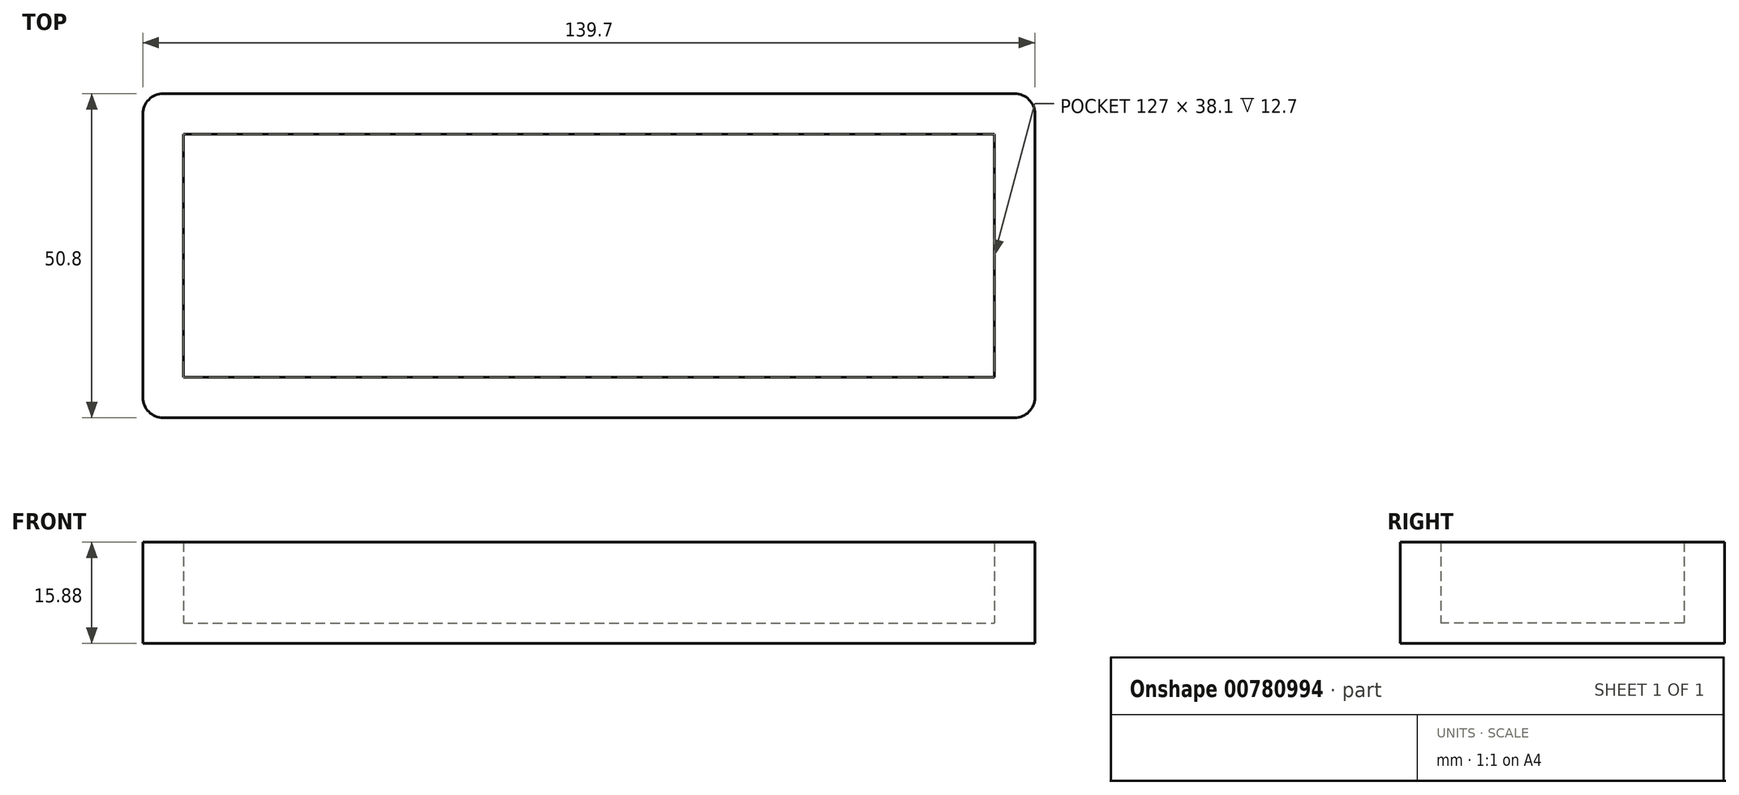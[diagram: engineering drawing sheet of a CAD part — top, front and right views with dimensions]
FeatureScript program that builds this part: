
annotation { "Feature Type Name" : "Feature", "Feature Type Description" : "" }
export const myFeature = defineFeature(function(context is Context, id is Id, definition is map)
    precondition{}
    {
        {
            var Q0;
            Q0=qCreatedBy(makeId("Top.planeOp"),FACE);
            var sketch = newSketch(context, id + "F0", { "sketchPlane" : qUnion([Q0])});
            skLineSegment(sketch, "E0.bottom", {"start": v(-64.83, 16.35) * mm, "end": v(74.87, 16.35) * mm});
            skLineSegment(sketch, "E0.top", {"start": v(-64.83, -34.45) * mm, "end": v(74.87, -34.45) * mm});
            skLineSegment(sketch, "E0.left", {"start": v(-64.83, 16.35) * mm, "end": v(-64.83, -34.45) * mm});
            skLineSegment(sketch, "E0.right", {"start": v(74.87, 16.35) * mm, "end": v(74.87, -34.45) * mm});
            skLineSegment(sketch, "E1", {"start": v(-64.83, 10) * mm, "end": v(-58.48, 10) * mm});
            skLineSegment(sketch, "E2", {"start": v(-58.48, 10) * mm, "end": v(-58.48, 16.35) * mm});
            skLineSegment(sketch, "E3", {"start": v(-58.48, 10) * mm, "end": v(74.87, 10) * mm});
            skLineSegment(sketch, "E4", {"start": v(-58.48, 10) * mm, "end": v(-58.48, -34.45) * mm});
            skLineSegment(sketch, "E5", {"start": v(-64.83, -34.45) * mm, "end": v(-64.83, -28.1) * mm});
            skLineSegment(sketch, "E6", {"start": v(-64.83, -28.1) * mm, "end": v(74.87, -28.1) * mm});
            skLineSegment(sketch, "E7", {"start": v(74.87, 16.35) * mm, "end": v(68.52, 16.35) * mm});
            skLineSegment(sketch, "E8", {"start": v(68.52, 16.35) * mm, "end": v(68.52, -34.45) * mm});
            skLineSegment(sketch, "E9", {"start": v(-58.48, 10) * mm, "end": v(68.52, -28.1) * mm});
            skSolve(sketch);
        }
        {
            var Q0;
            {var subQ0=sQuery(id+"F0.wireOp",EDGE,"E4");var subQ1=sQuery(id+"F0.wireOp",EDGE,"E0.top");var subQ2=makeQuery(id+"F0.imprint","INTERSECT",VERTEX,{"derivedFrom":[subQ1,subQ0]});var subQ15=sQuery(id+"F0.wireOp",EDGE,"E0.right");var subQ16=sQuery(id+"F0.wireOp",EDGE,"E0.bottom");var subQ17=makeQuery(id+"F0.imprint","INTERSECT",VERTEX,{"derivedFrom":[subQ16,subQ15]});var subQ19=sQuery(id+"F0.wireOp",EDGE,"E3");var subQ22=makeQuery(id+"F0.imprint","INTERSECT",VERTEX,{"derivedFrom":[subQ15,subQ19]});var subQ26=sQuery(id+"F0.wireOp",EDGE,"E2");var subQ28=makeQuery(id+"F0.imprint","IMPRINT",EDGE,{"derivedFrom":subQ26});var subQ29=sQuery(id+"F0.wireOp",EDGE,"E1");var subQ33=makeQuery(id+"F0.imprint","IMPRINT",EDGE,{"derivedFrom":subQ29});var subQ34=makeQuery(id+"F0.imprint","INTERSECT",VERTEX,{"derivedFrom":[subQ1,subQ15]});Q0=qUnion([makeQuery(id+"F0.imprint","IMPRINT",FACE,{"disambiguationData":[TD([[makeQuery(id+"F0.imprint","IMPRINT",EDGE,{"disambiguationData":[TD([[subQ34,1.0]])],"derivedFrom":subQ1}),1.0]])]}),makeQuery(id+"F0.imprint","IMPRINT",FACE,{"disambiguationData":[TD([[subQ33,-1.0]])]}),makeQuery(id+"F0.imprint","IMPRINT",FACE,{"disambiguationData":[TD([[subQ33,1.0]])]}),makeQuery(id+"F0.imprint","IMPRINT",FACE,{"disambiguationData":[TD([[subQ28,-1.0]])]}),makeQuery(id+"F0.imprint","IMPRINT",FACE,{"disambiguationData":[TD([[makeQuery(id+"F0.imprint","IMPRINT",EDGE,{"disambiguationData":[TD([[subQ22,-1.0]])],"derivedFrom":subQ15}),-1.0]])]}),makeQuery(id+"F0.imprint","IMPRINT",FACE,{"disambiguationData":[TD([[makeQuery(id+"F0.imprint","IMPRINT",EDGE,{"disambiguationData":[TD([[subQ17,1.0]])],"derivedFrom":subQ16}),-1.0]])]}),makeQuery(id+"F0.imprint","IMPRINT",FACE,{"disambiguationData":[TD([[makeQuery(id+"F0.imprint","IMPRINT",EDGE,{"disambiguationData":[TD([[subQ2,-1.0]])],"derivedFrom":subQ1}),1.0]])]}),makeQuery(id+"F0.imprint","IMPRINT",FACE,{"disambiguationData":[TD([[makeQuery(id+"F0.imprint","IMPRINT",EDGE,{"disambiguationData":[TD([[subQ2,1.0]])],"derivedFrom":subQ1}),1.0]])]})]);}
            extrude(context, id + "F1", {"entities" : qUnion([Q0]), "depth" : 12.7 * mm, "offsetDistance" : 25.4 * mm});
        }
        {
            var Q0;
            Q0=makeQuery(id+"F1.opExtrude","CAP_FACE",FACE,{"disambiguationData":[OSD([sQuery(id+"F0.wireOp",EDGE,"E0.bottom"),sQuery(id+"F0.wireOp",EDGE,"E0.top"),sQuery(id+"F0.wireOp",EDGE,"E0.left"),sQuery(id+"F0.wireOp",EDGE,"E0.right"),sQuery(id+"F0.wireOp",EDGE,"E3"),sQuery(id+"F0.wireOp",EDGE,"E4"),sQuery(id+"F0.wireOp",EDGE,"E6"),sQuery(id+"F0.wireOp",EDGE,"E8")])],"isStart":true});
            extrude(context, id + "F2", {"entities" : qUnion([Q0]), "operationType" : NewBodyOperationType.ADD, "depth" : 3.17 * mm, "offsetDistance" : 25.4 * mm});
        }
        {
            var Q0;
            {var subQ0=sQuery(id+"F0.wireOp",EDGE,"E9");Q0=makeQuery(id+"F0.imprint","IMPRINT",FACE,{"disambiguationData":[TD([[makeQuery(id+"F0.imprint","IMPRINT",EDGE,{"derivedFrom":subQ0}),1.0]])]});}
            var Q1;
            {var subQ0=sQuery(id+"F0.wireOp",EDGE,"E9");Q1=makeQuery(id+"F0.imprint","IMPRINT",FACE,{"disambiguationData":[TD([[makeQuery(id+"F0.imprint","IMPRINT",EDGE,{"derivedFrom":subQ0}),-1.0]])]});}
            extrude(context, id + "F3", {"entities" : qUnion([Q0, Q1]), "operationType" : NewBodyOperationType.ADD, "oppositeDirection" : true, "depth" : 3.17 * mm, "offsetDistance" : 25.4 * mm});
        }
        {
            var Q0;
            {var subQ0=sQuery(id+"F0.wireOp",EDGE,"E0.left");var subQ1=sQuery(id+"F0.wireOp",EDGE,"E0.top");Q0=makeQuery(id+"F2.boolean.opBoolean","MERGE",EDGE,{"derivedFrom":[makeQuery(id+"F1.opExtrude","SWEPT_EDGE",EDGE,{"disambiguationData":[OSD([subQ1,subQ0])]}),makeQuery(id+"F2.opExtrude","SWEPT_EDGE",EDGE,{"disambiguationData":[OSD([subQ1,subQ0])]})]});}
            var Q1;
            {var subQ0=sQuery(id+"F0.wireOp",EDGE,"E0.left");var subQ1=sQuery(id+"F0.wireOp",EDGE,"E0.bottom");Q1=makeQuery(id+"F2.boolean.opBoolean","MERGE",EDGE,{"derivedFrom":[makeQuery(id+"F1.opExtrude","SWEPT_EDGE",EDGE,{"disambiguationData":[OSD([subQ1,subQ0])]}),makeQuery(id+"F2.opExtrude","SWEPT_EDGE",EDGE,{"disambiguationData":[OSD([subQ1,subQ0])]})]});}
            var Q2;
            {var subQ0=sQuery(id+"F0.wireOp",EDGE,"E0.right");var subQ1=sQuery(id+"F0.wireOp",EDGE,"E0.top");Q2=makeQuery(id+"F2.boolean.opBoolean","MERGE",EDGE,{"derivedFrom":[makeQuery(id+"F1.opExtrude","SWEPT_EDGE",EDGE,{"disambiguationData":[OSD([subQ1,subQ0])]}),makeQuery(id+"F2.opExtrude","SWEPT_EDGE",EDGE,{"disambiguationData":[OSD([subQ1,subQ0])]})]});}
            var Q3;
            {var subQ0=sQuery(id+"F0.wireOp",EDGE,"E0.right");var subQ1=sQuery(id+"F0.wireOp",EDGE,"E0.bottom");Q3=makeQuery(id+"F2.boolean.opBoolean","MERGE",EDGE,{"derivedFrom":[makeQuery(id+"F1.opExtrude","SWEPT_EDGE",EDGE,{"disambiguationData":[OSD([subQ1,subQ0])]}),makeQuery(id+"F2.opExtrude","SWEPT_EDGE",EDGE,{"disambiguationData":[OSD([subQ1,subQ0])]})]});}
            fillet(context, id + "F4", {"entities" : qUnion([Q0, Q1, Q2, Q3]), "radius" : 3.17 * mm, "tangentPropagation" : true, "allowEdgeOverflow" : false});
        }
    });
